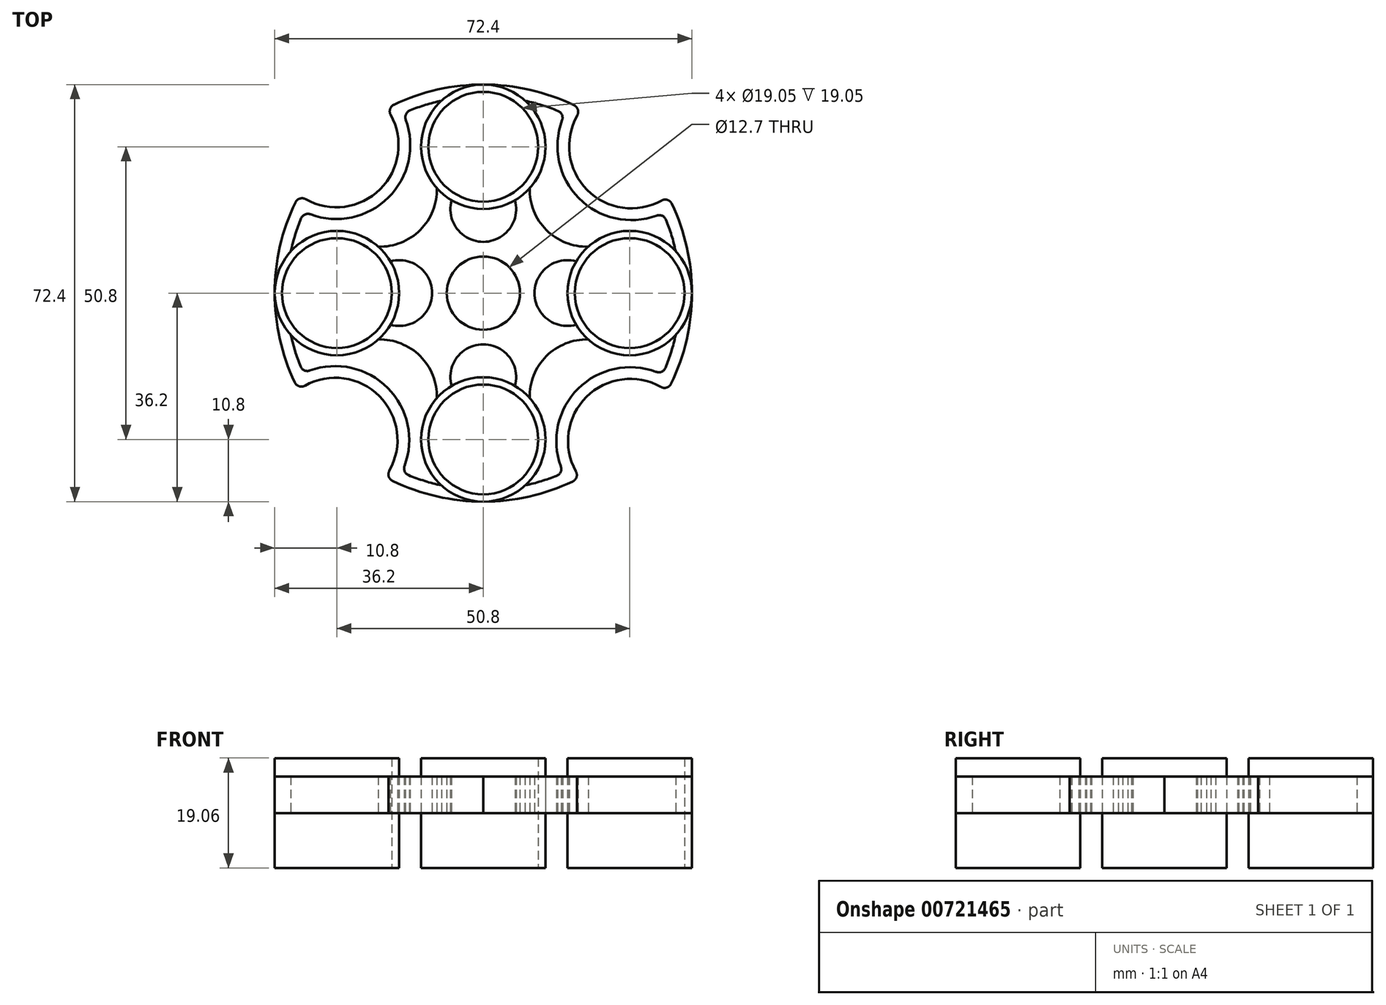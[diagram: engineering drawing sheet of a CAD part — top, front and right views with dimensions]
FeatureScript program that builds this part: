
annotation { "Feature Type Name" : "Feature", "Feature Type Description" : "" }
export const myFeature = defineFeature(function(context is Context, id is Id, definition is map)
    precondition{}
    {
        {
            var Q0;
            Q0=qCreatedBy(makeId("Top.planeOp"),FACE);
            var sketch = newSketch(context, id + "F0", { "sketchPlane" : qUnion([Q0])});
            skCircle(sketch, "E0", {"center": v(0, 0) * mm, "radius": 6.35 * mm});
            skCircle(sketch, "E1", {"center": v(0, 25.4) * mm, "radius": 9.53 * mm});
            skCircle(sketch, "E2", {"center": v(0, 25.4) * mm, "radius": 10.8 * mm});
            skPoint(sketch, "E3.visualSharp", {"position": v(21.9, 36.2) * mm});
            skCircle(sketch, "E4", {"center": v(0, 0) * mm, "radius": 8.9 * mm});
            skArc(sketch, "E5", {"start": v(15.74, 32.6) * mm, "mid": v(0.13, 36.2) * mm, "end": v(-15.5, 32.7) * mm});
            skLineSegment(sketch, "E6", {"start": v(0, -25.4) * mm, "end": v(0, 0) * mm});
            skCircle(sketch, "E7.1.2", {"center": v(-25.4, 0) * mm, "radius": 10.8 * mm});
            skCircle(sketch, "E7.1.3", {"center": v(-25.4, 0) * mm, "radius": 9.53 * mm});
            skCircle(sketch, "E7.2.2", {"center": v(0, -25.4) * mm, "radius": 10.8 * mm});
            skCircle(sketch, "E7.2.3", {"center": v(0, -25.4) * mm, "radius": 9.53 * mm});
            skCircle(sketch, "E7.3.2", {"center": v(25.4, 0) * mm, "radius": 10.8 * mm});
            skCircle(sketch, "E7.3.3", {"center": v(25.4, 0) * mm, "radius": 9.53 * mm});
            skArc(sketch, "E8", {"start": v(16.3, 30.82) * mm, "mid": v(18.02, 17.9) * mm, "end": v(30.94, 16.07) * mm});
            skArc(sketch, "E9.trimOffspring", {"start": v(8.05, 18.2) * mm, "mid": v(10.95, 10.95) * mm, "end": v(18.2, 8.05) * mm});
            skArc(sketch, "E10.0", {"start": v(13.67, 29.99) * mm, "mid": v(16.58, 16.46) * mm, "end": v(30.09, 13.45) * mm});
            skArc(sketch, "E10.1", {"start": v(12.96, 31.6) * mm, "mid": v(10.15, 32.62) * mm, "end": v(7.27, 33.38) * mm});
            skArc(sketch, "E11.trimOffspring", {"start": v(33.38, 7.27) * mm, "mid": v(32.66, 10.04) * mm, "end": v(31.7, 12.73) * mm});
            skArc(sketch, "E12.trimOffspring", {"start": v(0, 8.9) * mm, "mid": v(4.54, 11.14) * mm, "end": v(5.51, 16.12) * mm});
            skArc(sketch, "E13.trimOffspring", {"start": v(16.12, 5.51) * mm, "mid": v(11.14, 4.54) * mm, "end": v(8.9, 0) * mm});
            skPoint(sketch, "E14.visualSharp", {"position": v(17.02, 31.94) * mm});
            skArc(sketch, "E14.filletArc", {"start": v(16.3, 30.82) * mm, "mid": v(16.4, 31.83) * mm, "end": v(15.74, 32.6) * mm});
            skPoint(sketch, "E15.visualSharp", {"position": v(14.14, 31.1) * mm});
            skArc(sketch, "E15.filletArc", {"start": v(13.67, 29.99) * mm, "mid": v(13.64, 30.94) * mm, "end": v(12.96, 31.6) * mm});
            skPoint(sketch, "E16.visualSharp", {"position": v(32.06, 16.8) * mm});
            skArc(sketch, "E16.filletArc", {"start": v(32.7, 15.5) * mm, "mid": v(31.95, 16.17) * mm, "end": v(30.94, 16.07) * mm});
            skPoint(sketch, "E17.visualSharp", {"position": v(31.2, 13.92) * mm});
            skArc(sketch, "E17.filletArc", {"start": v(31.7, 12.73) * mm, "mid": v(31.04, 13.42) * mm, "end": v(30.09, 13.45) * mm});
            skArc(sketch, "E18.1.0", {"start": v(-8.9, 0) * mm, "mid": v(-11.14, 4.54) * mm, "end": v(-16.12, 5.51) * mm});
            skArc(sketch, "E18.1.1", {"start": v(-18.2, 8.05) * mm, "mid": v(-10.95, 10.95) * mm, "end": v(-8.05, 18.2) * mm});
            skArc(sketch, "E18.1.2", {"start": v(-5.51, 16.12) * mm, "mid": v(-4.54, 11.14) * mm, "end": v(0, 8.9) * mm});
            skArc(sketch, "E18.1.3", {"start": v(-31.6, 12.96) * mm, "mid": v(-32.62, 10.15) * mm, "end": v(-33.38, 7.27) * mm});
            skArc(sketch, "E18.1.4", {"start": v(-30.82, 16.3) * mm, "mid": v(-17.9, 18.02) * mm, "end": v(-16.07, 30.94) * mm});
            skArc(sketch, "E18.1.5", {"start": v(-29.99, 13.67) * mm, "mid": v(-16.46, 16.58) * mm, "end": v(-13.45, 30.09) * mm});
            skArc(sketch, "E18.1.6", {"start": v(-7.27, 33.38) * mm, "mid": v(-10.04, 32.66) * mm, "end": v(-12.73, 31.7) * mm});
            skArc(sketch, "E18.1.7", {"start": v(-12.73, 31.7) * mm, "mid": v(-13.42, 31.04) * mm, "end": v(-13.45, 30.09) * mm});
            skArc(sketch, "E18.1.8", {"start": v(-15.5, 32.7) * mm, "mid": v(-16.17, 31.95) * mm, "end": v(-16.07, 30.94) * mm});
            skArc(sketch, "E18.1.9", {"start": v(-30.82, 16.3) * mm, "mid": v(-31.83, 16.4) * mm, "end": v(-32.6, 15.74) * mm});
            skArc(sketch, "E18.2.0", {"start": v(0, -8.9) * mm, "mid": v(-4.54, -11.14) * mm, "end": v(-5.51, -16.12) * mm});
            skArc(sketch, "E18.2.1", {"start": v(-8.05, -18.2) * mm, "mid": v(-10.95, -10.95) * mm, "end": v(-18.2, -8.05) * mm});
            skArc(sketch, "E18.2.2", {"start": v(-16.12, -5.51) * mm, "mid": v(-11.14, -4.54) * mm, "end": v(-8.9, 0) * mm});
            skArc(sketch, "E18.2.3", {"start": v(-12.96, -31.6) * mm, "mid": v(-10.15, -32.62) * mm, "end": v(-7.27, -33.38) * mm});
            skArc(sketch, "E18.2.4", {"start": v(-16.3, -30.82) * mm, "mid": v(-18.02, -17.9) * mm, "end": v(-30.94, -16.07) * mm});
            skArc(sketch, "E18.2.5", {"start": v(-13.67, -29.99) * mm, "mid": v(-16.58, -16.46) * mm, "end": v(-30.09, -13.45) * mm});
            skArc(sketch, "E18.2.6", {"start": v(-33.38, -7.27) * mm, "mid": v(-32.66, -10.04) * mm, "end": v(-31.7, -12.73) * mm});
            skArc(sketch, "E18.2.7", {"start": v(-31.7, -12.73) * mm, "mid": v(-31.04, -13.42) * mm, "end": v(-30.09, -13.45) * mm});
            skArc(sketch, "E18.2.8", {"start": v(-32.7, -15.5) * mm, "mid": v(-31.95, -16.17) * mm, "end": v(-30.94, -16.07) * mm});
            skArc(sketch, "E18.2.9", {"start": v(-16.3, -30.82) * mm, "mid": v(-16.4, -31.83) * mm, "end": v(-15.74, -32.6) * mm});
            skArc(sketch, "E19.2.3.0", {"start": v(8.9, 0) * mm, "mid": v(11.14, -4.54) * mm, "end": v(16.12, -5.51) * mm});
            skArc(sketch, "E19.4.3.0", {"start": v(18.2, -8.05) * mm, "mid": v(10.95, -10.95) * mm, "end": v(8.05, -18.2) * mm});
            skArc(sketch, "E19.8.3.0", {"start": v(5.51, -16.12) * mm, "mid": v(4.54, -11.14) * mm, "end": v(0, -8.9) * mm});
            skArc(sketch, "E19.12.3.0", {"start": v(31.6, -12.96) * mm, "mid": v(32.62, -10.15) * mm, "end": v(33.38, -7.27) * mm});
            skArc(sketch, "E19.16.3.0", {"start": v(30.82, -16.3) * mm, "mid": v(17.9, -18.02) * mm, "end": v(16.07, -30.94) * mm});
            skArc(sketch, "E19.20.3.0", {"start": v(29.99, -13.67) * mm, "mid": v(16.46, -16.58) * mm, "end": v(13.45, -30.09) * mm});
            skArc(sketch, "E19.24.3.0", {"start": v(7.27, -33.38) * mm, "mid": v(10.04, -32.66) * mm, "end": v(12.73, -31.7) * mm});
            skArc(sketch, "E19.28.3.0", {"start": v(12.73, -31.7) * mm, "mid": v(13.42, -31.04) * mm, "end": v(13.45, -30.09) * mm});
            skArc(sketch, "E19.32.3.0", {"start": v(15.5, -32.7) * mm, "mid": v(16.17, -31.95) * mm, "end": v(16.07, -30.94) * mm});
            skArc(sketch, "E19.36.3.0", {"start": v(30.82, -16.3) * mm, "mid": v(31.83, -16.4) * mm, "end": v(32.6, -15.74) * mm});
            skArc(sketch, "E20.trimOffspring", {"start": v(-32.6, 15.74) * mm, "mid": v(-36.2, 0.13) * mm, "end": v(-32.7, -15.5) * mm});
            skArc(sketch, "E21.trimOffspring", {"start": v(-15.74, -32.6) * mm, "mid": v(-0.13, -36.2) * mm, "end": v(15.5, -32.7) * mm});
            skArc(sketch, "E22.trimOffspring", {"start": v(32.6, -15.74) * mm, "mid": v(36.2, -0.13) * mm, "end": v(32.7, 15.5) * mm});
            skPoint(sketch, "E23.orphan", {"position": v(31.6, -12.96) * mm});
            skPoint(sketch, "E24.orphan", {"position": v(29.99, -13.67) * mm});
            skPoint(sketch, "E25.orphan", {"position": v(-12.96, -31.6) * mm});
            skPoint(sketch, "E26.orphan", {"position": v(-13.67, -29.99) * mm});
            skPoint(sketch, "E27.orphan", {"position": v(-31.6, 12.96) * mm});
            skPoint(sketch, "E28.orphan", {"position": v(-29.99, 13.67) * mm});
            skPoint(sketch, "E29.visualSharp", {"position": v(-31.1, 14.14) * mm});
            skArc(sketch, "E29.filletArc", {"start": v(-29.99, 13.67) * mm, "mid": v(-30.94, 13.64) * mm, "end": v(-31.6, 12.96) * mm});
            skPoint(sketch, "E30.visualSharp", {"position": v(-14.14, -31.1) * mm});
            skArc(sketch, "E30.filletArc", {"start": v(-13.67, -29.99) * mm, "mid": v(-13.64, -30.94) * mm, "end": v(-12.96, -31.6) * mm});
            skPoint(sketch, "E31.visualSharp", {"position": v(31.1, -14.14) * mm});
            skArc(sketch, "E31.filletArc", {"start": v(29.99, -13.67) * mm, "mid": v(30.94, -13.64) * mm, "end": v(31.6, -12.96) * mm});
            skSolve(sketch);
        }
        {
            var Q0;
            {var subQ0=sQuery(id+"F0.wireOp",EDGE,"E18.1.0");Q0=makeQuery(id+"F0.imprint","IMPRINT",FACE,{"disambiguationData":[TD([[makeQuery(id+"F0.imprint","IMPRINT",EDGE,{"derivedFrom":subQ0}),-1.0]])]});}
            var Q1;
            {var subQ0=sQuery(id+"F0.wireOp",EDGE,"E9.trimOffspring");Q1=makeQuery(id+"F0.imprint","IMPRINT",FACE,{"disambiguationData":[TD([[makeQuery(id+"F0.imprint","IMPRINT",EDGE,{"derivedFrom":subQ0}),-1.0]])]});}
            var Q2;
            {var subQ0=sQuery(id+"F0.wireOp",EDGE,"E19.2.3.0");Q2=makeQuery(id+"F0.imprint","IMPRINT",FACE,{"disambiguationData":[TD([[makeQuery(id+"F0.imprint","IMPRINT",EDGE,{"derivedFrom":subQ0}),-1.0]])]});}
            var Q3;
            {var subQ0=sQuery(id+"F0.wireOp",EDGE,"E18.2.0");Q3=makeQuery(id+"F0.imprint","IMPRINT",FACE,{"disambiguationData":[TD([[makeQuery(id+"F0.imprint","IMPRINT",EDGE,{"derivedFrom":subQ0}),-1.0]])]});}
            var Q4;
            Q4=makeQuery(id+"F0.imprint","IMPRINT",FACE,{"disambiguationData":[TD([[makeQuery(id+"F0.imprint","IMPRINT",EDGE,{"derivedFrom":sQuery(id+"F0.wireOp",EDGE,"E0")}),-1.0]])]});
            var Q5;
            {var subQ9=sQuery(id+"F0.wireOp",EDGE,"E18.1.3");Q5=makeQuery(id+"F0.imprint","IMPRINT",FACE,{"disambiguationData":[TD([[makeQuery(id+"F0.imprint","IMPRINT",EDGE,{"derivedFrom":subQ9}),-1.0]])]});}
            var Q6;
            {var subQ2=sQuery(id+"F0.wireOp",EDGE,"E18.2.3");Q6=makeQuery(id+"F0.imprint","IMPRINT",FACE,{"disambiguationData":[TD([[makeQuery(id+"F0.imprint","IMPRINT",EDGE,{"derivedFrom":subQ2}),-1.0]])]});}
            var Q7;
            {var subQ5=sQuery(id+"F0.wireOp",EDGE,"E19.12.3.0");Q7=makeQuery(id+"F0.imprint","IMPRINT",FACE,{"disambiguationData":[TD([[makeQuery(id+"F0.imprint","IMPRINT",EDGE,{"derivedFrom":subQ5}),-1.0]])]});}
            var Q8;
            Q8=makeQuery(id+"F0.imprint","IMPRINT",FACE,{"disambiguationData":[TD([[makeQuery(id+"F0.imprint","IMPRINT",EDGE,{"derivedFrom":sQuery(id+"F0.wireOp",EDGE,"E8")}),-1.0]])]});
            extrude(context, id + "F1", {"entities" : qUnion([Q0, Q1, Q2, Q3, Q4, Q5, Q6, Q7, Q8]), "depth" : 6.35 * mm, "offsetDistance" : 25.4 * mm});
        }
        {
            var Q0;
            Q0=qCreatedBy(makeId("Top.planeOp"),FACE);
            var sketch = newSketch(context, id + "F2", { "sketchPlane" : qUnion([Q0])});
            skCircle(sketch, "E32", {"center": v(-25.4, 0) * mm, "radius": 10.8 * mm});
            skCircle(sketch, "E33", {"center": v(-25.4, 0) * mm, "radius": 9.53 * mm});
            skLineSegment(sketch, "E34", {"start": v(0, 0) * mm, "end": v(-25.4, 0) * mm});
            skCircle(sketch, "E35.1.0", {"center": v(0, -25.4) * mm, "radius": 9.53 * mm});
            skCircle(sketch, "E35.1.1", {"center": v(0, -25.4) * mm, "radius": 10.8 * mm});
            skCircle(sketch, "E35.2.0", {"center": v(25.4, 0) * mm, "radius": 9.53 * mm});
            skCircle(sketch, "E35.2.1", {"center": v(25.4, 0) * mm, "radius": 10.8 * mm});
            skPoint(sketch, "E35.center", {"position": v(0, 0) * mm});
            skCircle(sketch, "E36.1.3.0", {"center": v(0, 25.4) * mm, "radius": 9.53 * mm});
            skCircle(sketch, "E36.2.3.0", {"center": v(0, 25.4) * mm, "radius": 10.8 * mm});
            skSolve(sketch);
        }
        {
            var Q0;
            Q0 = qSketchRegion(id + "F2", true);
            extrude(context, id + "F3", {"entities" : qUnion([Q0]), "endBound" : BoundingType.SYMMETRIC, "depth" : 19.05 * mm, "offsetDistance" : 25.4 * mm});
        }
    });
